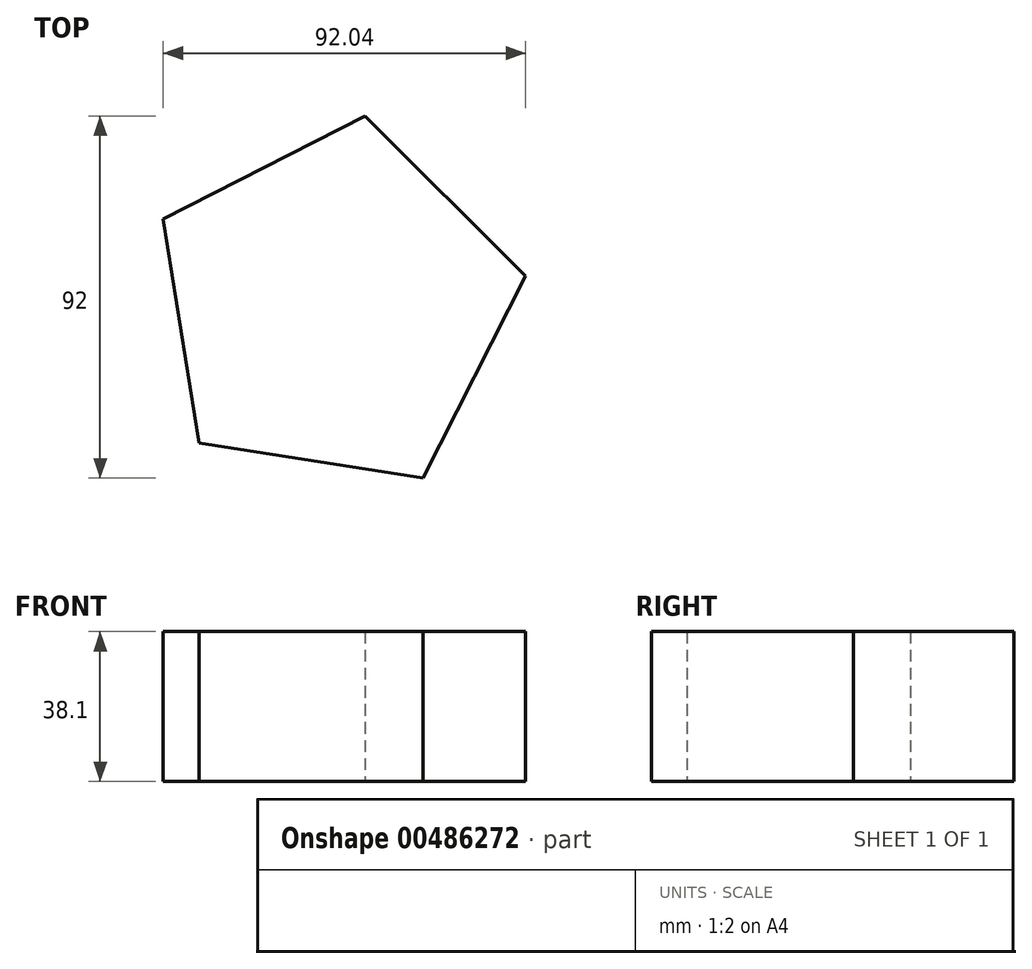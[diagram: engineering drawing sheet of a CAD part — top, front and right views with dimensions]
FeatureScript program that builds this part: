
annotation { "Feature Type Name" : "Feature", "Feature Type Description" : "" }
export const myFeature = defineFeature(function(context is Context, id is Id, definition is map)
    precondition{}
    {
        {
            var Q0;
            Q0=qCreatedBy(makeId("Top.planeOp"),FACE);
            var sketch = newSketch(context, id + "F0", { "sketchPlane" : qUnion([Q0])});
            skCircle(sketch, "E0.cCircle", {"center": v(-4.2, 17.95) * mm, "radius": 39.63 * mm, "construction": true});
            skLineSegment(sketch, "E0.0", {"start": v(44.17, 25.67) * mm, "end": v(18.08, -25.67) * mm});
            skLineSegment(sketch, "E0.1", {"start": v(18.08, -25.67) * mm, "end": v(-38.8, -16.72) * mm});
            skLineSegment(sketch, "E0.2", {"start": v(-38.8, -16.72) * mm, "end": v(-47.87, 40.14) * mm});
            skLineSegment(sketch, "E0.3", {"start": v(-47.87, 40.14) * mm, "end": v(3.4, 66.33) * mm});
            skLineSegment(sketch, "E0.4", {"start": v(3.4, 66.33) * mm, "end": v(44.17, 25.67) * mm});
            skPoint(sketch, "E0.0.midPoint", {"position": v(31.13, 0) * mm});
            skSolve(sketch);
        }
        {
            var Q0;
            Q0 = qSketchRegion(id + "F0", true);
            extrude(context, id + "F1", {"entities" : qUnion([Q0]), "depth" : 38.1 * mm});
        }
    });
